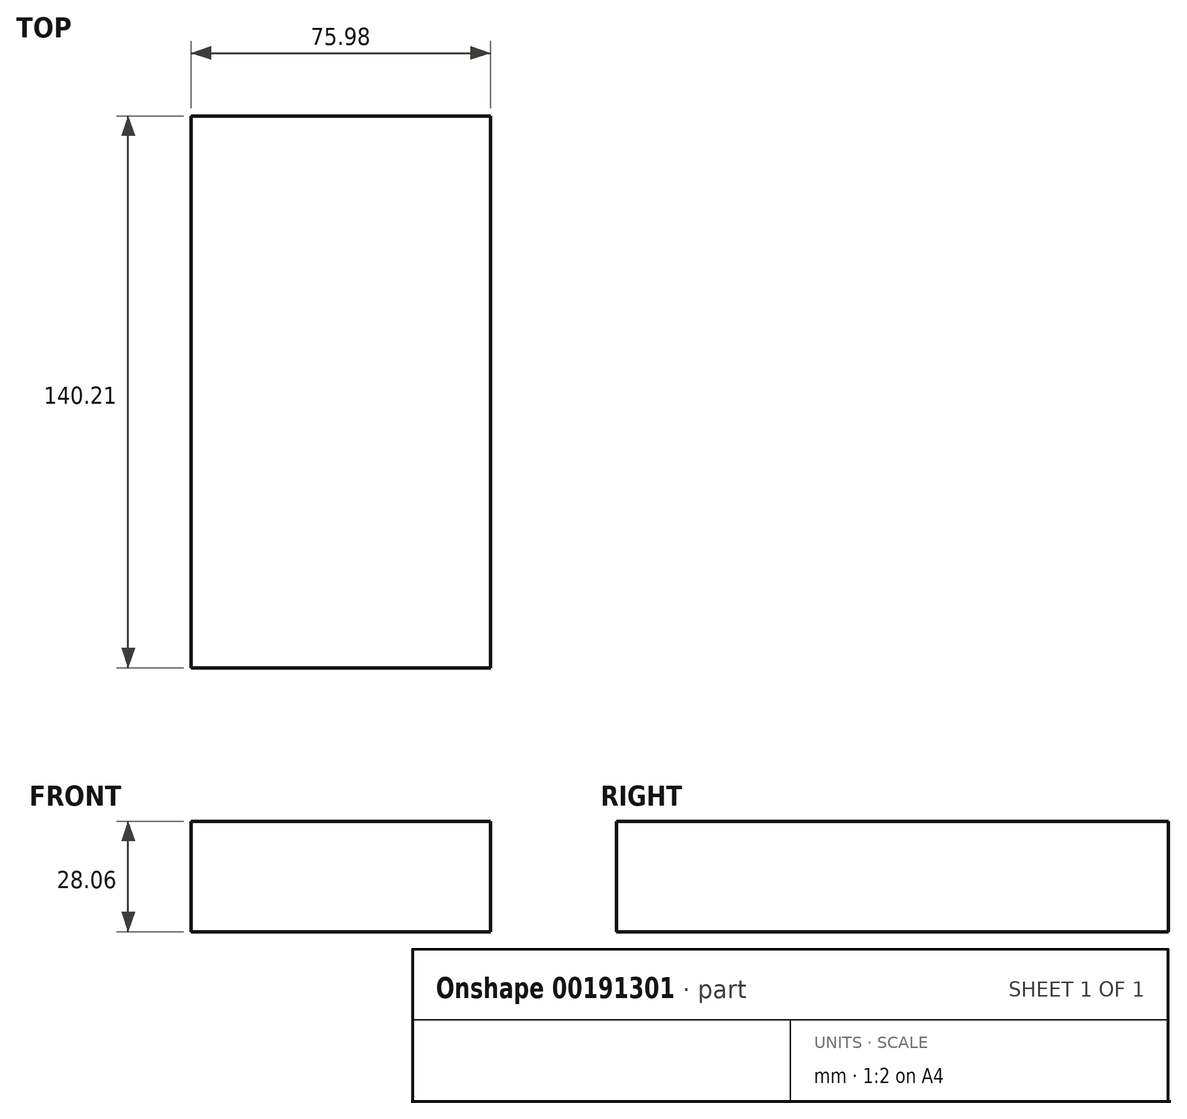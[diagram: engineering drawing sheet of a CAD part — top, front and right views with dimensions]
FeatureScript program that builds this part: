
annotation { "Feature Type Name" : "Feature", "Feature Type Description" : "" }
export const myFeature = defineFeature(function(context is Context, id is Id, definition is map)
    precondition{}
    {
        {
            var Q0;
            Q0=qCreatedBy(makeId("Front.planeOp"),FACE);
            var sketch = newSketch(context, id + "F0", { "sketchPlane" : qUnion([Q0])});
            skLineSegment(sketch, "E0", {"start": v(0, 0) * mm, "end": v(75.98, 0) * mm});
            skLineSegment(sketch, "E1", {"start": v(75.98, 0) * mm, "end": v(75.98, -28.06) * mm});
            skLineSegment(sketch, "E2", {"start": v(75.98, -28.06) * mm, "end": v(0, -28.06) * mm});
            skLineSegment(sketch, "E3", {"start": v(0, -28.06) * mm, "end": v(0, 0) * mm});
            skSolve(sketch);
        }
        {
            var Q0;
            Q0=makeQuery(id+"F0.imprint","IMPRINT",FACE,{"disambiguationData":[TD([[makeQuery(id+"F0.imprint","IMPRINT",EDGE,{"derivedFrom":sQuery(id+"F0.wireOp",EDGE,"E0")}),-1.0]])]});
            extrude(context, id + "F1", {"entities" : qUnion([Q0]), "depth" : 140.2 * mm});
        }
    });
